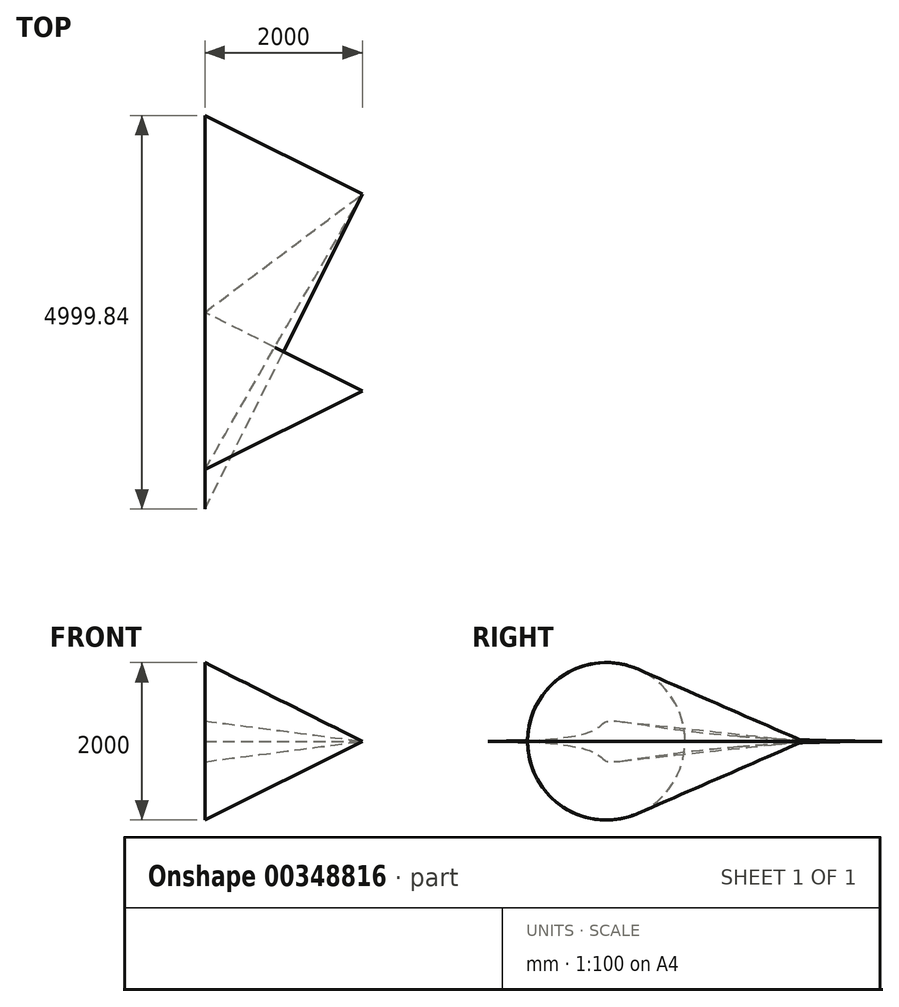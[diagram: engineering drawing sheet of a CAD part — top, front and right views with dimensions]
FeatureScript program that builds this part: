
annotation { "Feature Type Name" : "Feature", "Feature Type Description" : "" }
export const myFeature = defineFeature(function(context is Context, id is Id, definition is map)
    precondition{}
    {
        {
            var Q0;
            Q0=qCreatedBy(makeId("Right.planeOp"),FACE);
            var sketch = newSketch(context, id + "F0", { "sketchPlane" : qUnion([Q0])});
            skCircle(sketch, "E0", {"center": v(0, 0) * mm, "radius": 1000 * mm});
            skSolve(sketch);
        }
        {
            var Q0;
            Q0=qCreatedBy(makeId("Top.planeOp"),FACE);
            var sketch = newSketch(context, id + "F1", { "sketchPlane" : qUnion([Q0])});
            skLineSegment(sketch, "E1", {"start": v(0, 0) * mm, "end": v(2000, 0) * mm});
            skSolve(sketch);
        }
        {
            var Q0;
            Q0=makeQuery(id+"F0.imprint","IMPRINT",FACE,{"disambiguationData":[TD([[makeQuery(id+"F0.imprint","IMPRINT",EDGE,{"derivedFrom":sQuery(id+"F0.wireOp",EDGE,"E0")}),1.0]])]});
            var Q1;
            Q1=sQuery(id+"F1.wireOp",VERTEX,"E1.end");
            loft(context, id + "F2", {"sheetProfilesArray" : [{ "sheetProfileEntities" : qUnion([Q0]) }, { "sheetProfileEntities" : qUnion([Q1]) }]});
        }
        {
            var Q0;
            Q0=qCreatedBy(makeId("Top.planeOp"),FACE);
            var sketch = newSketch(context, id + "F3", { "sketchPlane" : qUnion([Q0])});
            skLineSegment(sketch, "E2", {"start": v(0, 0) * mm, "end": v(2000, 0) * mm});
            skLineSegment(sketch, "E3", {"start": v(2000, 0) * mm, "end": v(2000, 2500) * mm});
            skSolve(sketch);
        }
        {
            var Q0;
            Q0=makeQuery(id+"F0.imprint","IMPRINT",FACE,{"disambiguationData":[TD([[makeQuery(id+"F0.imprint","IMPRINT",EDGE,{"derivedFrom":sQuery(id+"F0.wireOp",EDGE,"E0")}),1.0]])]});
            var Q1;
            Q1=sQuery(id+"F3.wireOp",VERTEX,"E3.end");
            loft(context, id + "F4", {"sheetProfilesArray" : [{ "sheetProfileEntities" : qUnion([Q0]) }, { "sheetProfileEntities" : qUnion([Q1]) }]});
        }
        {
            var Q0;
            Q0=qCreatedBy(makeId("Right.planeOp"),FACE);
            var sketch = newSketch(context, id + "F5", { "sketchPlane" : qUnion([Q0])});
            skFitSpline(sketch, "E4", {"points": [v(-1500, 0) * mm, v(0, 250) * mm, v(3500, 0) * mm], "startDerivative": vector(11335.63, 0) * mm, "endDerivative": vector(12437.36, 0) * mm});
            skFitSpline(sketch, "E5", {"points": [v(-1500, 0) * mm, v(0, -250) * mm, v(3500, 0) * mm], "startDerivative": vector(11335.63, 0) * mm, "endDerivative": vector(12437.36, 0) * mm});
            skSolve(sketch);
        }
        {
            var Q0;
            {var subQ0=sQuery(id+"F5.wireOp",EDGE,"E4");Q0=makeQuery(id+"F5.imprint","IMPRINT",FACE,{"disambiguationData":[TD([[makeQuery(id+"F5.imprint","IMPRINT",EDGE,{"derivedFrom":subQ0}),-1.0]])]});}
            var Q1;
            Q1=sQuery(id+"F3.wireOp",VERTEX,"E3.end");
            loft(context, id + "F6", {"sheetProfilesArray" : [{ "sheetProfileEntities" : qUnion([Q0]) }, { "sheetProfileEntities" : qUnion([Q1]) }]});
        }
    });
